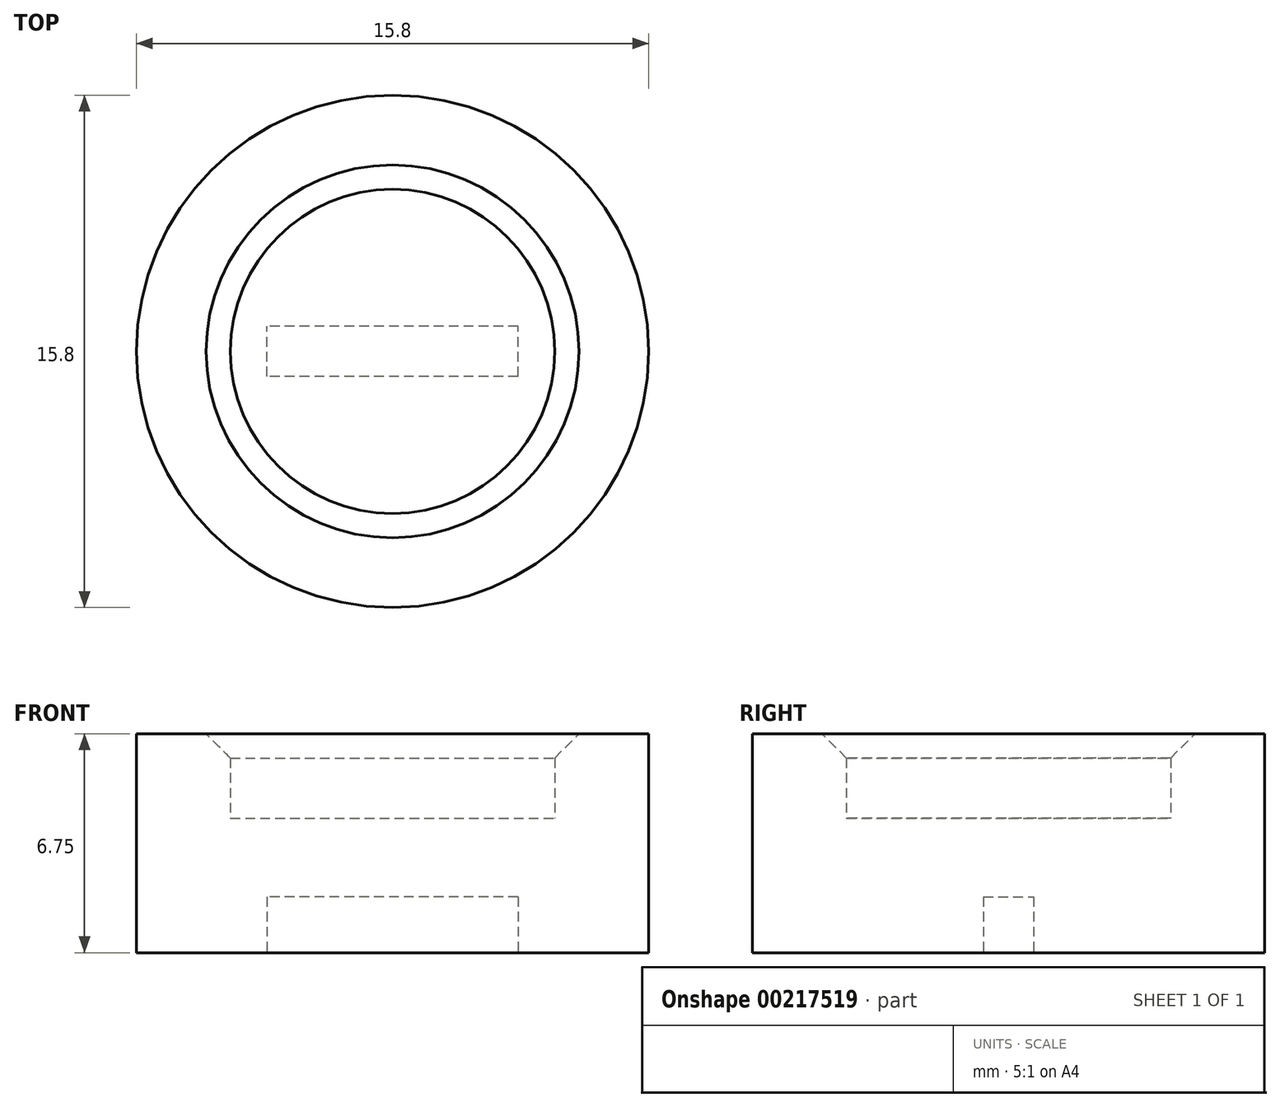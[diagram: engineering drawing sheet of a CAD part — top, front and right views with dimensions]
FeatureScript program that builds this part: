
annotation { "Feature Type Name" : "Feature", "Feature Type Description" : "" }
export const myFeature = defineFeature(function(context is Context, id is Id, definition is map)
    precondition{}
    {
        {
            var Q0;
            Q0=qCreatedBy(makeId("Front.planeOp"),FACE);
            var sketch = newSketch(context, id + "F0", { "sketchPlane" : qUnion([Q0])});
            skLineSegment(sketch, "E0.bottom", {"start": v(0, 0) * mm, "end": v(7.9, 0) * mm});
            skLineSegment(sketch, "E0.top", {"start": v(0, 4.15) * mm, "end": v(5, 4.15) * mm});
            skLineSegment(sketch, "E0.left", {"start": v(0, 0) * mm, "end": v(0, 4.15) * mm});
            skLineSegment(sketch, "E0.right", {"start": v(7.9, 0) * mm, "end": v(7.9, 4.15) * mm});
            skPoint(sketch, "E1.oppositeSnap0", {"position": v(7.9, 2.07) * mm});
            skLineSegment(sketch, "E1.bottom", {"start": v(5, 0) * mm, "end": v(7.9, 0) * mm});
            skLineSegment(sketch, "E1.top", {"start": v(5, 6.75) * mm, "end": v(7.9, 6.75) * mm});
            skLineSegment(sketch, "E1.left", {"start": v(5, 4.15) * mm, "end": v(5, 6.75) * mm});
            skLineSegment(sketch, "E1.right", {"start": v(7.9, 0) * mm, "end": v(7.9, 6.75) * mm});
            skSolve(sketch);
        }
        {
            var Q0;
            Q0 = qSketchRegion(id + "F0", true);
            var Q1;
            Q1=sQuery(id+"F0.wireOp",EDGE,"E0.left");
            revolve(context, id + "F1", {"entities" : qUnion([Q0]), "axis" : qUnion([Q1]), "revolveType" : RevolveType.FULL});
        }
        {
            var Q0;
            Q0=makeQuery(id+"F1.opRevolve","SWEPT_FACE",FACE,{"disambiguationData":[OSD([sQuery(id+"F0.wireOp",EDGE,"E0.bottom"),sQuery(id+"F0.wireOp",EDGE,"E1.bottom")])]});
            var sketch = newSketch(context, id + "F2", { "sketchPlane" : qUnion([Q0])});
            skLineSegment(sketch, "E2.bottom", {"start": v(3.88, 0.78) * mm, "end": v(-3.87, 0.78) * mm});
            skLineSegment(sketch, "E2.top", {"start": v(3.87, -0.78) * mm, "end": v(-3.88, -0.78) * mm});
            skLineSegment(sketch, "E2.left", {"start": v(3.88, 0.78) * mm, "end": v(3.87, -0.78) * mm});
            skLineSegment(sketch, "E2.right", {"start": v(-3.87, 0.78) * mm, "end": v(-3.88, -0.78) * mm});
            skPoint(sketch, "E2.middle", {"position": v(0, 0) * mm});
            skSolve(sketch);
        }
        {
            var Q0;
            Q0 = qSketchRegion(id + "F2", true);
            extrude(context, id + "F3", {"entities" : qUnion([Q0]), "operationType" : NewBodyOperationType.REMOVE, "oppositeDirection" : true, "depth" : 1.72 * mm});
        }
        {
            var Q0;
            Q0=makeQuery(id+"F1.opRevolve","SWEPT_EDGE",EDGE,{"disambiguationData":[OSD([sQuery(id+"F0.wireOp",EDGE,"E1.top"),sQuery(id+"F0.wireOp",EDGE,"E1.left")])]});
            chamfer(context, id + "F4", {"entities" : qUnion([Q0]), "width" : 0.75 * mm, "tangentPropagation" : true});
        }
    });
